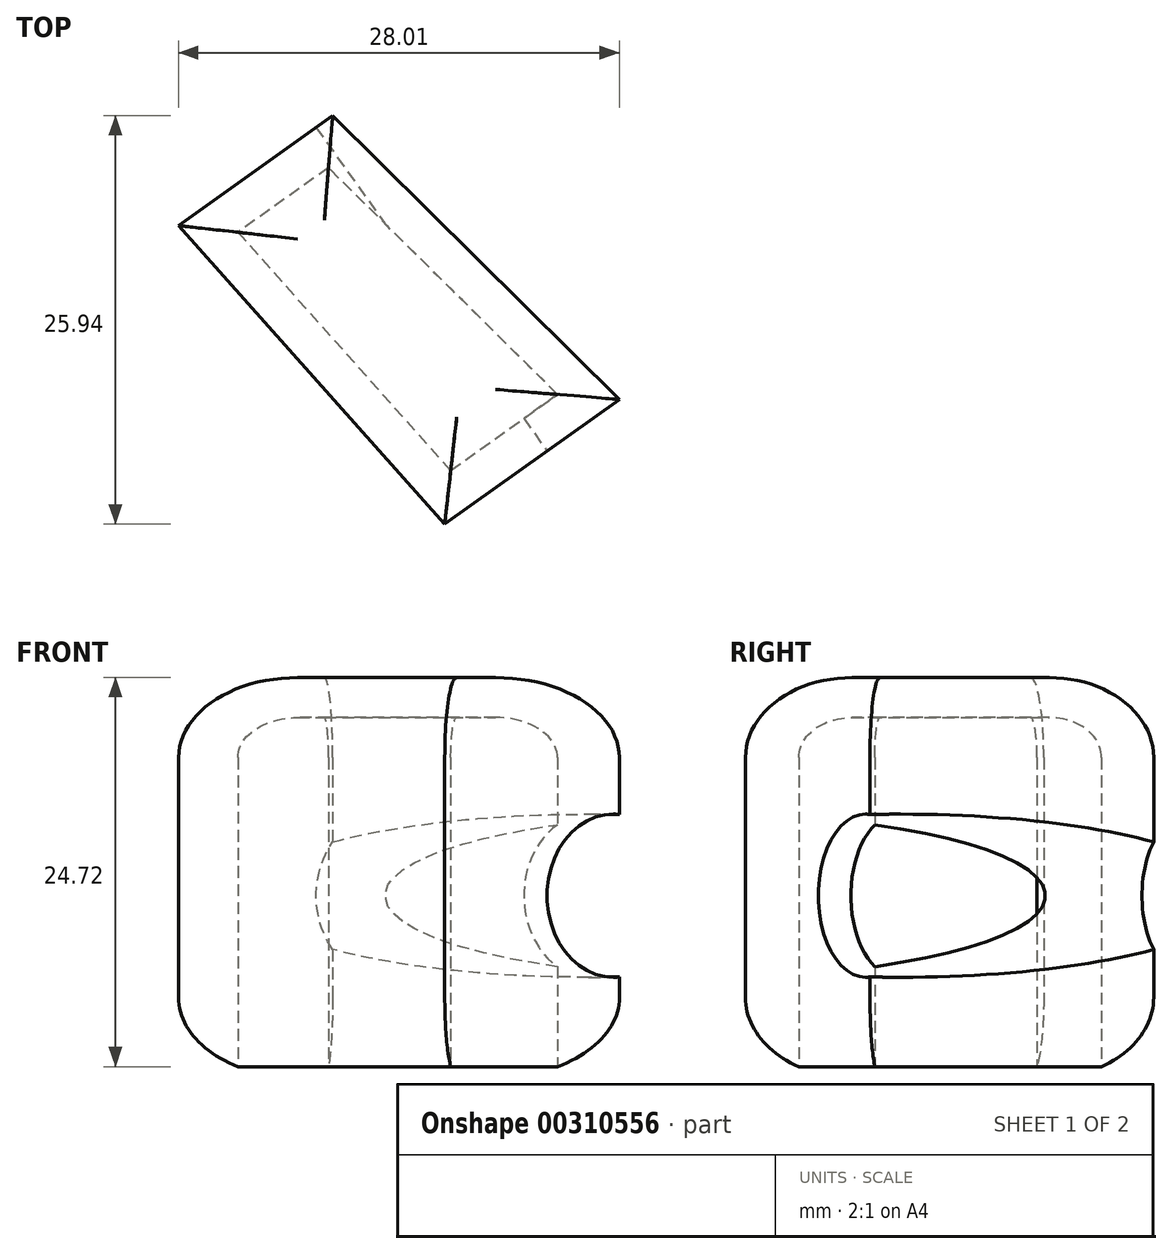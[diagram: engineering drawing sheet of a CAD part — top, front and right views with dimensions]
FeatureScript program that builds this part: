
annotation { "Feature Type Name" : "Feature", "Feature Type Description" : "" }
export const myFeature = defineFeature(function(context is Context, id is Id, definition is map)
    precondition{}
    {
        {
            var Q0;
            Q0=qCreatedBy(makeId("Top.planeOp"),FACE);
            var sketch = newSketch(context, id + "F0", { "sketchPlane" : qUnion([Q0])});
            skLineSegment(sketch, "E0", {"start": v(-33.03, 5.57) * mm, "end": v(15.54, -46.4) * mm});
            skLineSegment(sketch, "E1", {"start": v(15.54, -46.4) * mm, "end": v(45.1, -12.95) * mm});
            skLineSegment(sketch, "E2", {"start": v(45.1, -12.95) * mm, "end": v(-1.4, 28.12) * mm});
            skLineSegment(sketch, "E3", {"start": v(-1.4, 28.12) * mm, "end": v(-33.03, 5.57) * mm});
            skLineSegment(sketch, "E4", {"start": v(-10.7, 1.12) * mm, "end": v(-0.9, 8.1) * mm});
            skLineSegment(sketch, "E5", {"start": v(-0.9, 8.1) * mm, "end": v(17.31, -9.92) * mm});
            skLineSegment(sketch, "E6", {"start": v(17.31, -9.92) * mm, "end": v(6.22, -17.83) * mm});
            skLineSegment(sketch, "E7", {"start": v(6.22, -17.83) * mm, "end": v(-10.7, 1.12) * mm});
            skSolve(sketch);
        }
        {
            var Q0;
            Q0=makeQuery(id+"F0.imprint","IMPRINT",FACE,{"disambiguationData":[TD([[makeQuery(id+"F0.imprint","IMPRINT",EDGE,{"derivedFrom":sQuery(id+"F0.wireOp",EDGE,"E4")}),-1.0]])]});
            extrude(context, id + "F1", {"entities" : qUnion([Q0]), "depth" : 25.4 * mm});
        }
        {
            var Q0;
            Q0=makeQuery(id+"F1.opExtrude","CAP_EDGE",EDGE,{"disambiguationData":[OSD([sQuery(id+"F0.wireOp",EDGE,"E5")])],"isStart":false});
            var Q1;
            Q1=makeQuery(id+"F1.opExtrude","CAP_EDGE",EDGE,{"disambiguationData":[OSD([sQuery(id+"F0.wireOp",EDGE,"E6")])],"isStart":false});
            var Q2;
            Q2=makeQuery(id+"F1.opExtrude","CAP_EDGE",EDGE,{"disambiguationData":[OSD([sQuery(id+"F0.wireOp",EDGE,"E7")])],"isStart":false});
            var Q3;
            Q3=makeQuery(id+"F1.opExtrude","CAP_EDGE",EDGE,{"disambiguationData":[OSD([sQuery(id+"F0.wireOp",EDGE,"E4")])],"isStart":false});
            fillet(context, id + "F2", {"entities" : qUnion([Q0, Q1, Q2, Q3]), "radius" : 5.08 * mm, "tangentPropagation" : true, "allowEdgeOverflow" : false});
        }
        {
            var Q0;
            Q0=makeQuery(id+"F1.opExtrude","CAP_FACE",FACE,{"disambiguationData":[OSD([sQuery(id+"F0.wireOp",EDGE,"E4"),sQuery(id+"F0.wireOp",EDGE,"E5"),sQuery(id+"F0.wireOp",EDGE,"E6"),sQuery(id+"F0.wireOp",EDGE,"E7")])],"isStart":true});
            shell(context, id + "F3", {"entities" : qUnion([Q0]), "thickness" : 2.54 * mm});
        }
        {
            var Q0;
            Q0=makeQuery(id+"F1.opExtrude","CAP_EDGE",EDGE,{"disambiguationData":[OSD([sQuery(id+"F0.wireOp",EDGE,"E7")])],"isStart":true});
            var Q1;
            Q1=makeQuery(id+"F1.opExtrude","CAP_EDGE",EDGE,{"disambiguationData":[OSD([sQuery(id+"F0.wireOp",EDGE,"E6")])],"isStart":true});
            var Q2;
            Q2=makeQuery(id+"F1.opExtrude","CAP_EDGE",EDGE,{"disambiguationData":[OSD([sQuery(id+"F0.wireOp",EDGE,"E5")])],"isStart":true});
            var Q3;
            Q3=makeQuery(id+"F1.opExtrude","CAP_EDGE",EDGE,{"disambiguationData":[OSD([sQuery(id+"F0.wireOp",EDGE,"E4")])],"isStart":true});
            fillet(context, id + "F4", {"entities" : qUnion([Q0, Q1, Q2, Q3]), "radius" : 5.08 * mm, "tangentPropagation" : true, "allowEdgeOverflow" : false});
        }
        {
            var Q0;
            Q0=makeQuery(id+"F1.opExtrude","SWEPT_FACE",FACE,{"disambiguationData":[OSD([sQuery(id+"F0.wireOp",EDGE,"E6")])]});
            var sketch = newSketch(context, id + "F5", { "sketchPlane" : qUnion([Q0])});
            skCircle(sketch, "E8", {"center": v(7.87, 11.54) * mm, "radius": 5.18 * mm});
            skSolve(sketch);
        }
        {
            var Q0;
            Q0=makeQuery(id+"F5.imprint","IMPRINT",FACE,{"disambiguationData":[TD([[makeQuery(id+"F5.imprint","IMPRINT",EDGE,{"derivedFrom":sQuery(id+"F5.wireOp",EDGE,"E8")}),1.0]])]});
            var Q1;
            Q1=sQuery(id+"F5.wireOp",EDGE,"E8");
            extrude(context, id + "F6", {"entities" : qUnion([Q0]), "operationType" : NewBodyOperationType.REMOVE, "surfaceEntities" : qUnion([Q1]), "oppositeDirection" : true, "depth" : 105.66 * mm});
        }
    });
